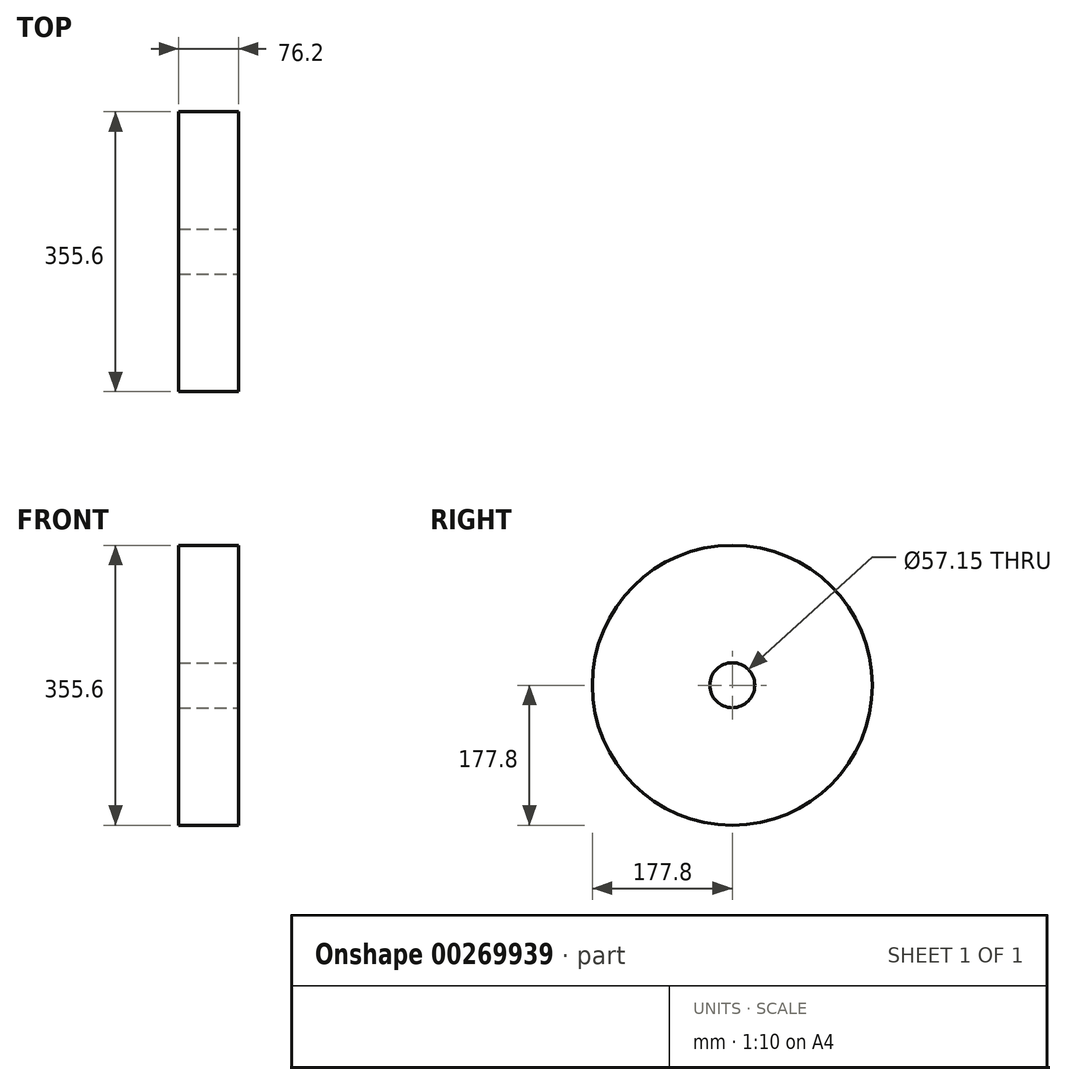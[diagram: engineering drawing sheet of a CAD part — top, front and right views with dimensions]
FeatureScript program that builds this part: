
annotation { "Feature Type Name" : "Feature", "Feature Type Description" : "" }
export const myFeature = defineFeature(function(context is Context, id is Id, definition is map)
    precondition{}
    {
        {
            var Q0;
            Q0=qCreatedBy(makeId("Right.planeOp"),FACE);
            var sketch = newSketch(context, id + "F0", { "sketchPlane" : qUnion([Q0])});
            skCircle(sketch, "E0", {"center": v(0, 0) * mm, "radius": 177.8 * mm});
            skSolve(sketch);
        }
        {
            var Q0;
            Q0 = qSketchRegion(id + "F0", true);
            extrude(context, id + "F1", {"entities" : qUnion([Q0]), "depth" : 76.2 * mm});
        }
        {
            var Q0;
            Q0=makeQuery(id+"F1.opExtrude","CAP_FACE",FACE,{"disambiguationData":[OSD([sQuery(id+"F0.wireOp",EDGE,"E0")])],"isStart":false});
            var sketch = newSketch(context, id + "F2", { "sketchPlane" : qUnion([Q0])});
            skCircle(sketch, "E1", {"center": v(0, 0) * mm, "radius": 28.58 * mm});
            skSolve(sketch);
        }
        {
            var Q0;
            Q0=makeQuery(id+"F2.imprint","IMPRINT",FACE,{"disambiguationData":[TD([[makeQuery(id+"F2.imprint","IMPRINT",EDGE,{"derivedFrom":sQuery(id+"F2.wireOp",EDGE,"E1")}),1.0]])]});
            extrude(context, id + "F3", {"entities" : qUnion([Q0]), "operationType" : NewBodyOperationType.REMOVE, "endBound" : BoundingType.THROUGH_ALL, "oppositeDirection" : true, "depth" : 25.4 * mm});
        }
    });
